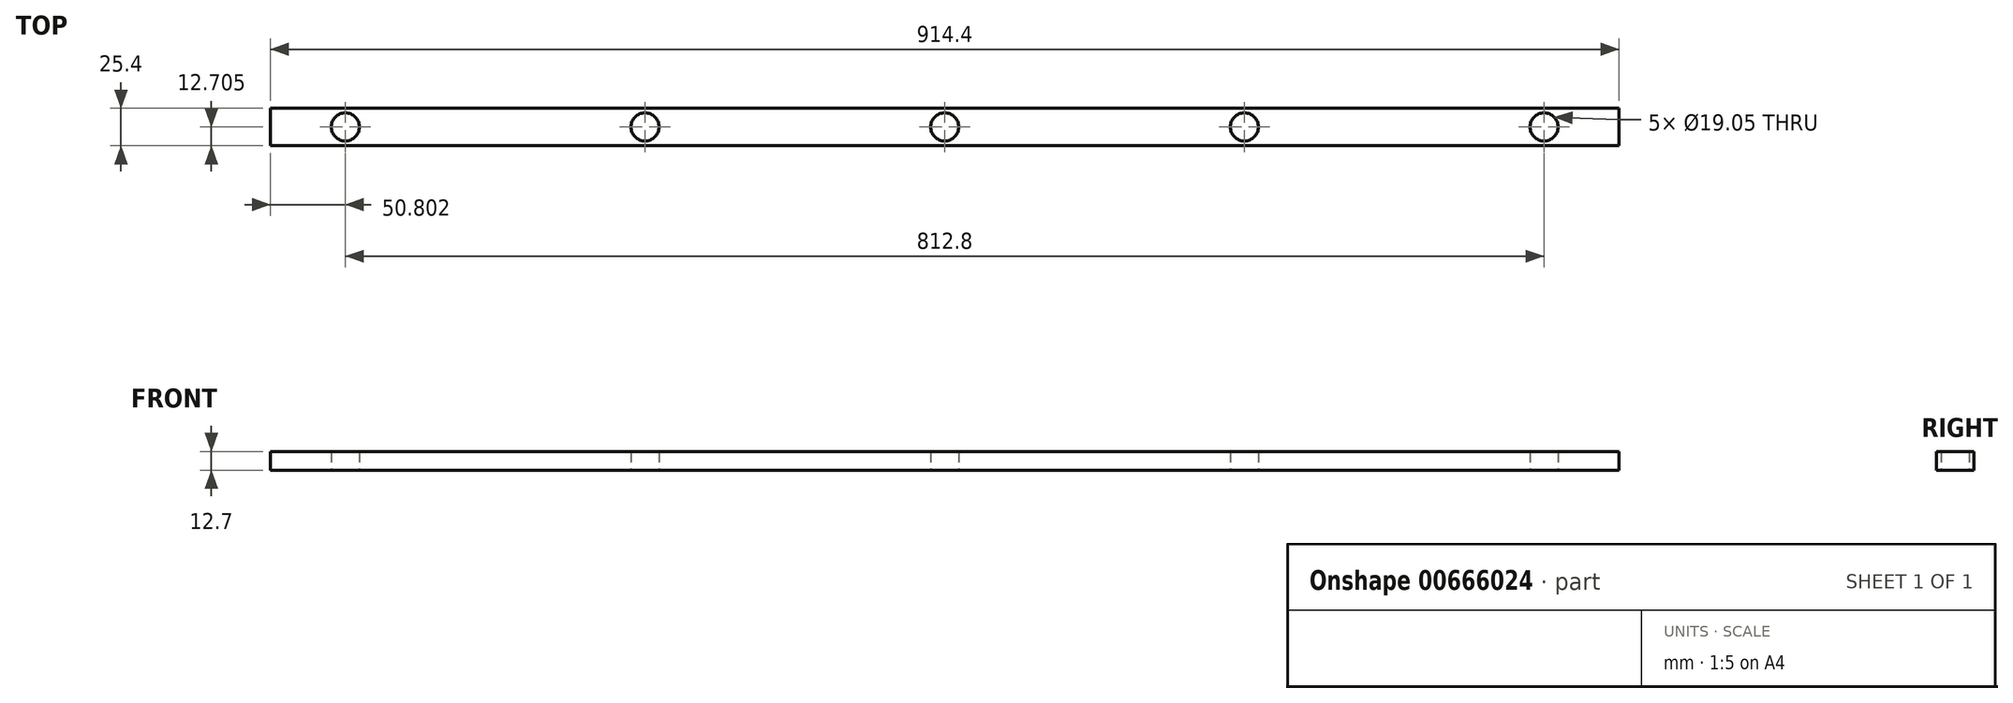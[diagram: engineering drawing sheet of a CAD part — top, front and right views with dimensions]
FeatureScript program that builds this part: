
annotation { "Feature Type Name" : "Feature", "Feature Type Description" : "" }
export const myFeature = defineFeature(function(context is Context, id is Id, definition is map)
    precondition{}
    {
        {
            var Q0;
            Q0=qCreatedBy(makeId("Top.planeOp"),FACE);
            var sketch = newSketch(context, id + "F0", { "sketchPlane" : qUnion([Q0])});
            skLineSegment(sketch, "E0.bottom", {"start": v(-142.65, 27.4) * mm, "end": v(771.75, 27.4) * mm});
            skLineSegment(sketch, "E0.top", {"start": v(-142.65, 2) * mm, "end": v(771.75, 2) * mm});
            skLineSegment(sketch, "E0.left", {"start": v(-142.65, 27.4) * mm, "end": v(-142.65, 2) * mm});
            skLineSegment(sketch, "E0.right", {"start": v(771.75, 27.4) * mm, "end": v(771.75, 2) * mm});
            skLineSegment(sketch, "E1", {"start": v(314.55, 27.4) * mm, "end": v(314.55, 2) * mm, "construction": true});
            skLineSegment(sketch, "E2.0", {"start": v(-142.65, 14.7) * mm, "end": v(771.75, 14.7) * mm, "construction": true});
            skCircle(sketch, "E3", {"center": v(314.55, 14.7) * mm, "radius": 9.53 * mm});
            skLineSegment(sketch, "E4.0", {"start": v(111.35, 27.4) * mm, "end": v(111.35, 2) * mm, "construction": true});
            skLineSegment(sketch, "E5.0", {"start": v(517.75, 27.4) * mm, "end": v(517.75, 2) * mm, "construction": true});
            skCircle(sketch, "E6", {"center": v(111.35, 14.7) * mm, "radius": 9.53 * mm});
            skCircle(sketch, "E7", {"center": v(517.75, 14.7) * mm, "radius": 9.53 * mm});
            skLineSegment(sketch, "E8.0", {"start": v(-91.85, 27.4) * mm, "end": v(-91.85, 2) * mm, "construction": true});
            skCircle(sketch, "E9", {"center": v(-91.85, 14.7) * mm, "radius": 9.53 * mm});
            skLineSegment(sketch, "E10.0", {"start": v(720.95, 27.4) * mm, "end": v(720.95, 2) * mm, "construction": true});
            skCircle(sketch, "E11", {"center": v(720.95, 14.7) * mm, "radius": 9.53 * mm});
            skSolve(sketch);
        }
        {
            var Q0;
            Q0=makeQuery(id+"F0.imprint","IMPRINT",FACE,{"disambiguationData":[TD([[makeQuery(id+"F0.imprint","IMPRINT",EDGE,{"derivedFrom":sQuery(id+"F0.wireOp",EDGE,"E0.bottom")}),-1.0]])]});
            extrude(context, id + "F1", {"entities" : qUnion([Q0]), "depth" : 12.7 * mm, "offsetDistance" : 25.4 * mm});
        }
    });
